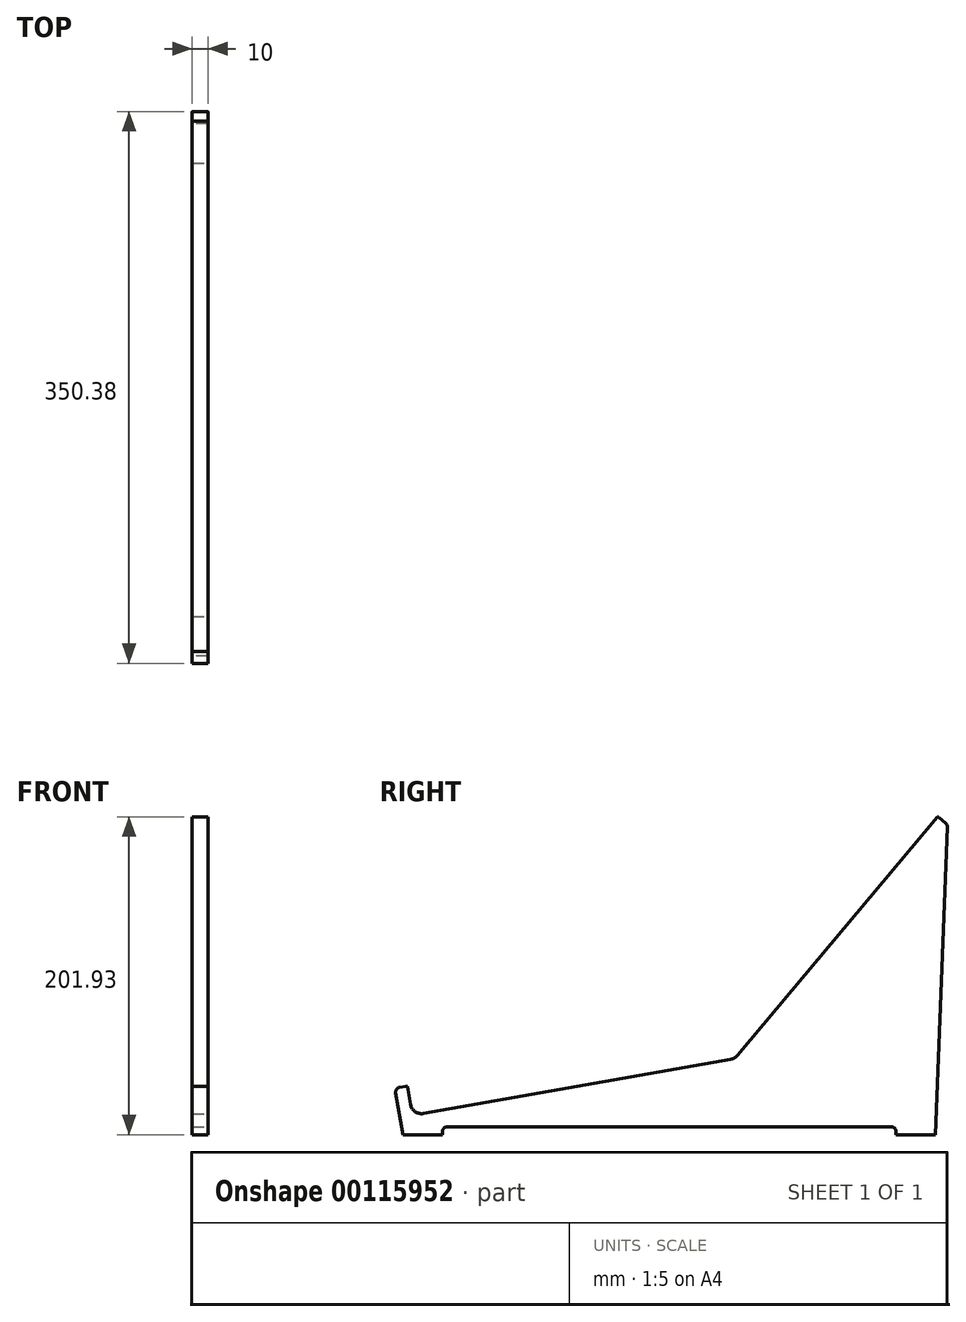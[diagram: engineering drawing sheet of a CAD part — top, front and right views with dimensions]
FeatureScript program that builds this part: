
annotation { "Feature Type Name" : "Feature", "Feature Type Description" : "" }
export const myFeature = defineFeature(function(context is Context, id is Id, definition is map)
    precondition{}
    {
        {
            var Q0;
            Q0=qCreatedBy(makeId("Right.planeOp"),FACE);
            var sketch = newSketch(context, id + "F0", { "sketchPlane" : qUnion([Q0])});
            skLineSegment(sketch, "E0", {"start": v(-338.03, 0) * mm, "end": v(0, 0) * mm});
            skLineSegment(sketch, "E1", {"start": v(0, 0) * mm, "end": v(0, 0) * mm});
            skLineSegment(sketch, "E2", {"start": v(-128.56, 50.14) * mm, "end": v(0, 203.35) * mm});
            skLineSegment(sketch, "E3", {"start": v(-128.56, 50.14) * mm, "end": v(-330.44, 14.54) * mm});
            skLineSegment(sketch, "E4", {"start": v(-330.44, 14.54) * mm, "end": v(-333.4, 31.28) * mm});
            skLineSegment(sketch, "E5", {"start": v(-333.4, 31.28) * mm, "end": v(-343.24, 29.54) * mm});
            skLineSegment(sketch, "E6", {"start": v(-343.24, 29.54) * mm, "end": v(-338.03, 0) * mm});
            skLineSegment(sketch, "E7", {"start": v(0, 203.35) * mm, "end": v(7.66, 196.92) * mm});
            skLineSegment(sketch, "E8", {"start": v(7.66, 196.92) * mm, "end": v(0, 0) * mm});
            skSolve(sketch);
        }
        {
            var Q0;
            Q0=makeQuery(id+"F0.imprint","IMPRINT",FACE,{"disambiguationData":[TD([[makeQuery(id+"F0.imprint","IMPRINT",EDGE,{"derivedFrom":sQuery(id+"F0.wireOp",EDGE,"E0")}),1.0]])]});
            extrude(context, id + "F1", {"entities" : qUnion([Q0]), "depth" : 10 * mm, "offsetDistance" : 25 * mm});
        }
        {
            var Q0;
            Q0=makeQuery(id+"F1.opExtrude","CAP_FACE",FACE,{"disambiguationData":[OSD([sQuery(id+"F0.wireOp",EDGE,"E0"),sQuery(id+"F0.wireOp",EDGE,"E2"),sQuery(id+"F0.wireOp",EDGE,"E3"),sQuery(id+"F0.wireOp",EDGE,"E4"),sQuery(id+"F0.wireOp",EDGE,"E5"),sQuery(id+"F0.wireOp",EDGE,"E6"),sQuery(id+"F0.wireOp",EDGE,"E7"),sQuery(id+"F0.wireOp",EDGE,"E8")])],"isStart":false});
            var sketch = newSketch(context, id + "F2", { "sketchPlane" : qUnion([Q0])});
            skLineSegment(sketch, "E9.bottom", {"start": v(-313.03, 0) * mm, "end": v(-25, 0) * mm});
            skLineSegment(sketch, "E9.top", {"start": v(-313.03, 5) * mm, "end": v(-25, 5) * mm});
            skLineSegment(sketch, "E9.left", {"start": v(-313.03, 0) * mm, "end": v(-313.03, 5) * mm});
            skLineSegment(sketch, "E9.right", {"start": v(-25, 0) * mm, "end": v(-25, 5) * mm});
            skSolve(sketch);
        }
        {
            var Q0;
            Q0 = qSketchRegion(id + "F2", true);
            extrude(context, id + "F3", {"entities" : qUnion([Q0]), "operationType" : NewBodyOperationType.REMOVE, "endBound" : BoundingType.THROUGH_ALL, "oppositeDirection" : true, "depth" : 25 * mm, "offsetDistance" : 25 * mm});
        }
        {
            var Q0;
            Q0=makeQuery(id+"F1.opExtrude","SWEPT_EDGE",EDGE,{"disambiguationData":[OSD([sQuery(id+"F0.wireOp",EDGE,"E2"),sQuery(id+"F0.wireOp",EDGE,"E7")])]});
            var Q1;
            Q1=makeQuery(id+"F1.opExtrude","SWEPT_EDGE",EDGE,{"disambiguationData":[OSD([sQuery(id+"F0.wireOp",EDGE,"E7"),sQuery(id+"F0.wireOp",EDGE,"E8")])]});
            var Q2;
            Q2=makeQuery(id+"F3.boolean.opBoolean","COPY",EDGE,{"derivedFrom":makeQuery(id+"F3.opExtrude","SWEPT_EDGE",EDGE,{"disambiguationData":[OSD([sQuery(id+"F2.wireOp",EDGE,"E9.top"),sQuery(id+"F2.wireOp",EDGE,"E9.right")])]})});
            var Q3;
            Q3=makeQuery(id+"F3.boolean.opBoolean","COPY",EDGE,{"derivedFrom":makeQuery(id+"F3.opExtrude","SWEPT_EDGE",EDGE,{"disambiguationData":[OSD([sQuery(id+"F2.wireOp",EDGE,"E9.top"),sQuery(id+"F2.wireOp",EDGE,"E9.left")])]})});
            var Q4;
            Q4=makeQuery(id+"F1.opExtrude","SWEPT_EDGE",EDGE,{"disambiguationData":[OSD([sQuery(id+"F0.wireOp",EDGE,"E4"),sQuery(id+"F0.wireOp",EDGE,"E5")])]});
            var Q5;
            Q5=makeQuery(id+"F1.opExtrude","SWEPT_EDGE",EDGE,{"disambiguationData":[OSD([sQuery(id+"F0.wireOp",EDGE,"E5"),sQuery(id+"F0.wireOp",EDGE,"E6")])]});
            fillet(context, id + "F4", {"entities" : qUnion([Q0, Q1, Q2, Q3, Q4, Q5]), "radius" : 3 * mm, "tangentPropagation" : true, "allowEdgeOverflow" : false});
        }
        {
            var Q0;
            Q0=makeQuery(id+"F1.opExtrude","SWEPT_EDGE",EDGE,{"disambiguationData":[OSD([sQuery(id+"F0.wireOp",EDGE,"E3"),sQuery(id+"F0.wireOp",EDGE,"E4")])]});
            var Q1;
            Q1=makeQuery(id+"F1.opExtrude","SWEPT_EDGE",EDGE,{"disambiguationData":[OSD([sQuery(id+"F0.wireOp",EDGE,"E2"),sQuery(id+"F0.wireOp",EDGE,"E3")])]});
            fillet(context, id + "F5", {"entities" : qUnion([Q0, Q1]), "radius" : 5 * mm, "tangentPropagation" : true, "allowEdgeOverflow" : false});
        }
        {
            var Q0;
            Q0=makeQuery(id+"F1.opExtrude","CAP_FACE",FACE,{"disambiguationData":[OSD([sQuery(id+"F0.wireOp",EDGE,"E0"),sQuery(id+"F0.wireOp",EDGE,"E2"),sQuery(id+"F0.wireOp",EDGE,"E3"),sQuery(id+"F0.wireOp",EDGE,"E4"),sQuery(id+"F0.wireOp",EDGE,"E5"),sQuery(id+"F0.wireOp",EDGE,"E6"),sQuery(id+"F0.wireOp",EDGE,"E7"),sQuery(id+"F0.wireOp",EDGE,"E8")])],"isStart":false});
            var sketch = newSketch(context, id + "F6", { "sketchPlane" : qUnion([Q0])});
            skLineSegment(sketch, "E10.0", {"start": v(-333.28, 19.12) * mm, "end": v(-336.35, 36.52) * mm});
            skLineSegment(sketch, "E10.1", {"start": v(-125.86, 50.25) * mm, "end": v(5.13, 206.35) * mm});
            skArc(sketch, "E10.2", {"start": v(-125.86, 50.25) * mm, "mid": v(-127.72, 48.68) * mm, "end": v(-130, 47.85) * mm});
            skLineSegment(sketch, "E10.3", {"start": v(-130, 47.85) * mm, "end": v(-325.17, 13.44) * mm});
            skArc(sketch, "E10.4", {"start": v(-325.17, 13.44) * mm, "mid": v(-330.4, 14.6) * mm, "end": v(-333.28, 19.12) * mm});
            skLineSegment(sketch, "E11", {"start": v(-336.35, 36.52) * mm, "end": v(5.13, 206.35) * mm});
            skSolve(sketch);
        }
        {
            var Q0;
            Q0 = qSketchRegion(id + "F6", true);
            extrude(context, id + "F7", {"entities" : qUnion([Q0]), "operationType" : NewBodyOperationType.REMOVE, "oppositeDirection" : true, "depth" : 25 * mm, "offsetDistance" : 25 * mm});
        }
    });
